# Revit family: Reece_Tap_Wolfen_Timed Flow Push Button_Hob Mounted
name_source: partatom
category: Plumbing Fixtures
revit_build: Autodesk Revit 2018 (Build: 20180329_1100(x64)
units: mm (PartAtom-declared; Revit-internal decimal feet)

## family parameters
Cut with Voids When Loaded = No
Host = Face
Part Type = Normal
Room Calculation Point = Yes
Round Connector Dimension = Use Diameter
Shared = Yes

## types (1)
- Chrome
    CWFU = 0
    Default Elevation = 1000 mm  [stored 3.28084 ft]
    Description = Wolfen Hob Bubbler Timed Flow Push Button Chrome
    Disclaimer = THIS FILE IS THE PROPERTY OF THE REECE GROUP. IT MAY NOT BE REPRODUCED, REVERSE-ENGINEERED OR MODIFIED. ANY REPUBLICATION, TRANSMISSION OR DISTRIBUTION FOR THE PURPOSE OF COMMERCIALLY EXPLOITING THE FILES IS PROHIBITED.
    HWFU = 0
    Keynote = Product #252419, Reece_Tap_Wolfen_Timed Flow Push Button_Hob Mounted - Chrome
    Manufacturer = Wolfen
    Model = Wolfen
    Reece_Detail_Additional = Timed Flow Push Button
    Reece_Detail_Disclaimer = THIS FILE IS THE PROPERTY OF THE REECE GROUP. IT MAY NOT BE REPRODUCED, REVERSE-ENGINEERED OR MODIFIED. ANY REPUBLICATION, TRANSMISSION OR DISTRIBUTION FOR THE PURPOSE OF COMMERCIALLY EXPLOITING THE FILES IS PROHIBITED.
    Reece_Material_Colour = Reece_Brass_Brushed
    Reece_Material_Main = Reece_Brass_Chrome
    Reece_Material_Secondary = Reece_Rubber_Blue
    Reece_Overall_Height = 163 mm
    Reece_Product_Brand = Wolfen
    Reece_Product_Description = Wolfen Hob Bubbler Timed Flow Push Button Chrome (6 Star)
    Reece_Product_Mount = Hob Mounted
    Reece_Product_Number = 252419
    Reece_Product_Sub Brand = Wolfen
    Reece_Product_Type = Tap
    Reece_Product_Web Page = https://www.reece.com.au
    Reece_Tap_Clearance = 146 mm
    Reece_Tap_Inlet = 12 mm  [stored 0.0393701 ft]
    Type Comments = Tap
    URL = https://www.reece.com.au
    WFU = 0

note: [stored X ft] marks values corroborated as IEEE doubles in the binary element streams (Revit-internal decimal feet)

## geometry (parser evidence)
native form markers: Sweep x4
no freeform markers — native parametric forms only
